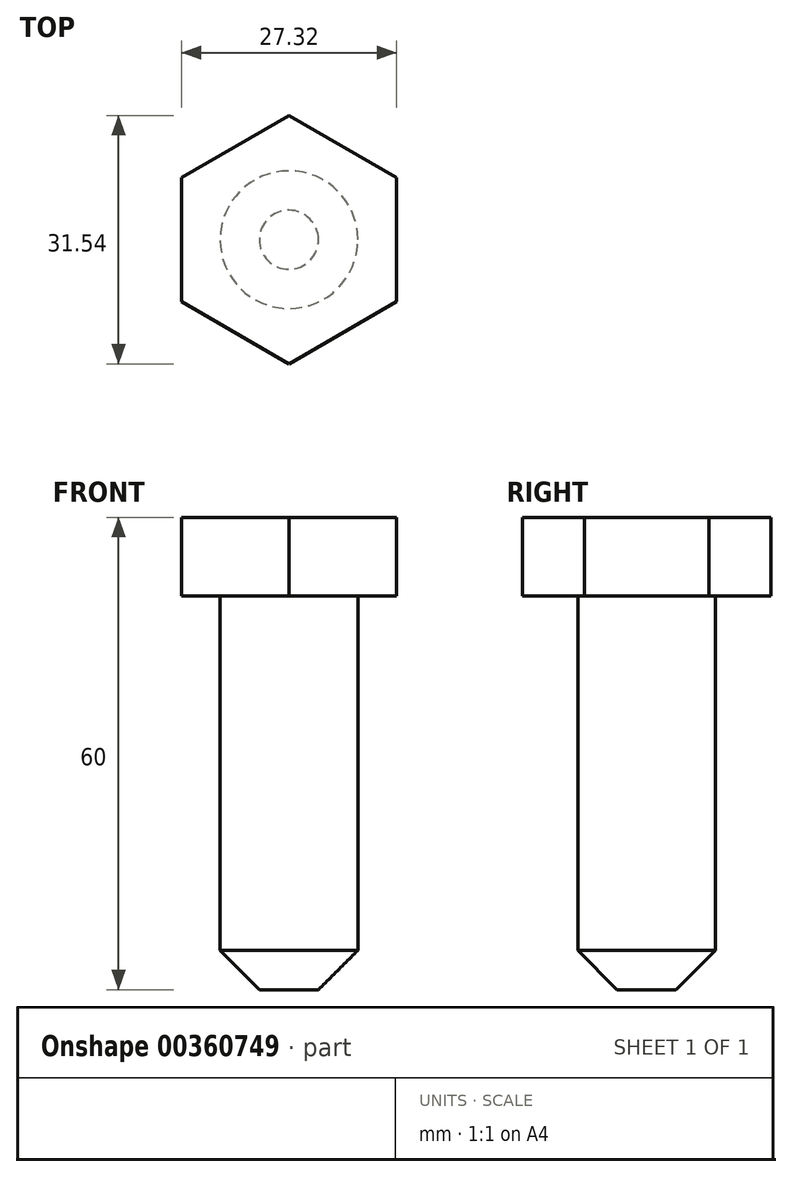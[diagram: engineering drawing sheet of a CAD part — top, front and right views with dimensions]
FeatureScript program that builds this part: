
annotation { "Feature Type Name" : "Feature", "Feature Type Description" : "" }
export const myFeature = defineFeature(function(context is Context, id is Id, definition is map)
    precondition{}
    {
        {
            var Q0;
            Q0=qCreatedBy(makeId("Top.planeOp"),FACE);
            var sketch = newSketch(context, id + "F0", { "sketchPlane" : qUnion([Q0])});
            skCircle(sketch, "E0", {"center": v(0, 0) * mm, "radius": 8.75 * mm});
            skCircle(sketch, "E1.cCircle", {"center": v(0, 0) * mm, "radius": 13.66 * mm, "construction": true});
            skLineSegment(sketch, "E1.0", {"start": v(13.66, 7.88) * mm, "end": v(13.66, -7.88) * mm});
            skLineSegment(sketch, "E1.1", {"start": v(13.66, -7.88) * mm, "end": v(0, -15.77) * mm});
            skLineSegment(sketch, "E1.2", {"start": v(0, -15.77) * mm, "end": v(-13.66, -7.88) * mm});
            skLineSegment(sketch, "E1.3", {"start": v(-13.66, -7.88) * mm, "end": v(-13.66, 7.88) * mm});
            skLineSegment(sketch, "E1.4", {"start": v(-13.66, 7.88) * mm, "end": v(0, 15.77) * mm});
            skLineSegment(sketch, "E1.5", {"start": v(0, 15.77) * mm, "end": v(13.66, 7.88) * mm});
            skPoint(sketch, "E1.0.midPoint", {"position": v(13.66, 0) * mm});
            skSolve(sketch);
        }
        {
            var Q0;
            Q0=makeQuery(id+"F0.imprint","IMPRINT",FACE,{"disambiguationData":[TD([[makeQuery(id+"F0.imprint","IMPRINT",EDGE,{"derivedFrom":sQuery(id+"F0.wireOp",EDGE,"E0")}),1.0]])]});
            extrude(context, id + "F1", {"entities" : qUnion([Q0]), "oppositeDirection" : true, "depth" : 60 * mm});
        }
        {
            var Q0;
            Q0=makeQuery(id+"F0.imprint","IMPRINT",FACE,{"disambiguationData":[TD([[makeQuery(id+"F0.imprint","IMPRINT",EDGE,{"derivedFrom":sQuery(id+"F0.wireOp",EDGE,"E0")}),-1.0]])]});
            var Q1;
            Q1=makeQuery(id+"F0.imprint","IMPRINT",FACE,{"disambiguationData":[TD([[makeQuery(id+"F0.imprint","IMPRINT",EDGE,{"derivedFrom":sQuery(id+"F0.wireOp",EDGE,"E0")}),1.0]])]});
            extrude(context, id + "F2", {"entities" : qUnion([Q0, Q1]), "operationType" : NewBodyOperationType.ADD, "oppositeDirection" : true, "depth" : 10 * mm});
        }
        {
            var Q0;
            Q0=makeQuery(id+"F1.opExtrude","CAP_EDGE",EDGE,{"disambiguationData":[OSD([sQuery(id+"F0.wireOp",EDGE,"E0")])],"isStart":false});
            chamfer(context, id + "F3", {"entities" : qUnion([Q0]), "width" : 5 * mm, "tangentPropagation" : true});
        }
    });
